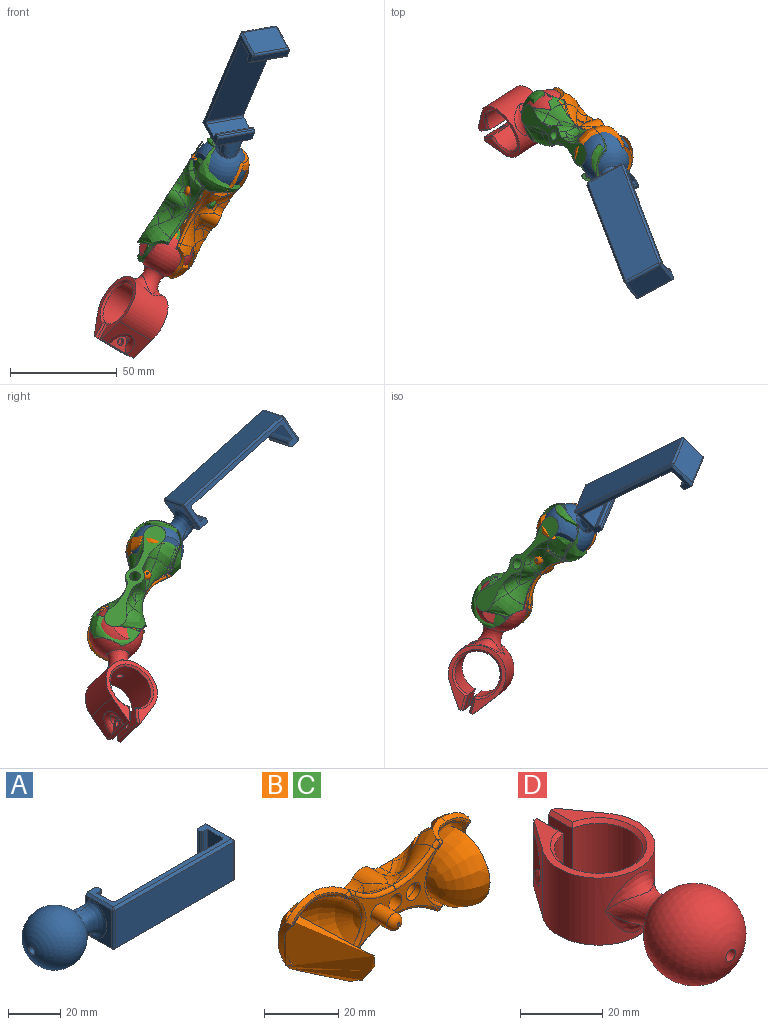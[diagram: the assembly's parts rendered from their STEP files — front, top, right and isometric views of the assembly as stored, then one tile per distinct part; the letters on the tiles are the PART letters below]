
ASSEMBLY  parts=4 mates=4
PART A: 46 faces, bbox 98.6x25.9x25.9 mm
  f0: plane 18.06x11.56mm, normal (-1,0,0), area 79.7mm2, adj f19,f29,f36,f45
  f1: plane 5.66x3.37mm, normal (-1,0,0), area 4.8mm2, adj f8,f20,f45
  f2: sphere r=12.5mm, area 1668.1mm2, adj f3,f18,f19,f20,f21,f22
  f3: plane 15x15mm, normal (0,0,-1), area 176.7mm2, adj f2
  f4: plane 5.66x3.37mm, normal (-1,0,0), area 4.8mm2, adj f8,f21,f36
  f5: plane 20x8mm, normal (1,0,0), area 160mm2, adj f6,f16,f17,f35
  f6: plane 20x2mm, normal (0,-1,0), area 40mm2, adj f5,f16,f17,f27
  f7: plane 20x1mm, normal (1,0,0), area 20mm2, adj f16,f17,f27,f28
  f8: plane 20x5mm, normal (0,1,0), area 99mm2, adj f1,f4,f16,f17,f18,f28,f36,f45
  f9: plane 64x18mm, normal (0,-1,0), area 1152mm2, adj f29,f30,f38,f43
  f10: plane 18x13mm, normal (1,0,0), area 234mm2, adj f30,f31,f40,f41
  f11: plane 20x4mm, normal (0,1,0), area 80mm2, adj f16,f17,f31,f32
  f12: plane 20x1mm, normal (-1,0,0), area 20mm2, adj f16,f17,f32,f33
  f13: plane 20x2mm, normal (0,-1,0), area 40mm2, adj f14,f16,f17,f33
  f14: plane 20x8mm, normal (-1,0,0), area 160mm2, adj f13,f16,f17,f34
  f15: plane 58x20mm, normal (0,1,0), area 1160mm2, adj f16,f17,f34,f35
  f16: plane 64x14mm, normal (0,0,1), area 193.6mm2, adj f5,f6,f7,f8,f11,f12,f13,f14
  f17: plane 64x14mm, normal (0,0,-1), area 193.6mm2, adj f5,f6,f7,f8,f11,f12,f13,f14
  f18: bspline ~14.32x8mm, area 52.9mm2, adj f2,f8,f20,f21
  f19: bspline ~18x13.55mm, area 213.6mm2, adj f0,f2,f20,f21
  f20: bspline ~11.31x8.33mm, area 31.4mm2, adj f1,f2,f18,f19
  f21: bspline ~11.31x8.33mm, area 31.4mm2, adj f2,f4,f18,f19
  f22: cone r=1.62mm half-angle=3deg, axis (-1,0,0), area 33.7mm2, adj f2,f23
  f23: sphere r=9mm, area 804.6mm2, adj f22,f24,f25
  f24: plane 8.83x8.83mm, normal (-1,0,0), area 60.2mm2, adj f23,f26
  f25: plane 12.45x12.45mm, normal (0,0,1), area 121.7mm2, adj f23
  f26: cone r=1.62mm half-angle=3deg, axis (-1,0,0), area 18.7mm2, adj f24
  f27: cylinder r=1mm len=20mm, axis (0,0,1), area 31.4mm2, adj f6,f7,f16,f17
  f28: cylinder r=1mm len=20mm, axis (0,0,-1), area 31.4mm2, adj f7,f8,f16,f17
  f29: cylinder r=1mm len=18mm, axis (0,0,-1), area 28.3mm2, adj f0,f9,f37,f44
  f30: cylinder r=1mm len=18mm, axis (0,0,-1), area 28.3mm2, adj f9,f10,f39,f42
  f31: cylinder r=1mm len=20mm, axis (0,0,-1), area 29.8mm2, adj f10,f11,f40,f41
  f32: cylinder r=1mm len=20mm, axis (0,0,-1), area 31.4mm2, adj f11,f12,f16,f17
  f33: cylinder r=1mm len=20mm, axis (0,0,1), area 31.4mm2, adj f12,f13,f16,f17
  f34: cylinder r=1mm len=20mm, axis (0,0,1), area 31.4mm2, adj f14,f15,f16,f17
  f35: cylinder r=1mm len=20mm, axis (0,0,1), area 31.4mm2, adj f5,f15,f16,f17
  f36: plane 14x1mm, normal (-0.71,0,0.71), area 19.8mm2, adj f0,f4,f8,f16,f37
  f37: cone r=1mm half-angle=45deg, axis (0,0,-1), area 1.1mm2, adj f29,f36,f38
  f38: plane 64x1mm, normal (0,-0.71,0.71), area 90.5mm2, adj f9,f16,f37,f39
  f39: cone r=1mm half-angle=45deg, axis (0,0,-1), area 1.1mm2, adj f30,f38,f40
  f40: plane 14.42x1.42mm, normal (0.71,0,0.71), area 19.5mm2, adj f10,f16,f31,f39
  f41: plane 14.42x1.42mm, normal (0.71,0,-0.71), area 19.5mm2, adj f10,f17,f31,f42
  f42: cone r=1mm half-angle=45deg, axis (0,0,1), area 1.1mm2, adj f30,f41,f43
  f43: plane 64x1mm, normal (0,-0.71,-0.71), area 90.5mm2, adj f9,f17,f42,f44
  f44: cone r=1mm half-angle=45deg, axis (0,0,1), area 1.1mm2, adj f29,f43,f45
  f45: plane 14x1mm, normal (-0.71,0,-0.71), area 19.8mm2, adj f0,f1,f8,f17,f44
PART B: 88 faces, bbox 71.9x25.8x27.9 mm
  f0: cylinder r=0.5mm len=1mm, axis (0,-1,0), area 0.2mm2, adj f86,f87
  f1: plane 59.78x10.4mm, normal (0,-1,0), area 338mm2, adj f2,f3,f8,f14,f15,f16,f17,f19
  f2: plane 4.98x3.76mm, normal (0,0,-1), area 10.1mm2, adj f1,f17,f18,f19
  f3: plane 4.98x3.76mm, normal (0,0,1), area 10.1mm2, adj f1,f22,f23,f24
  f4: revolved ~14.78x8.77mm, area 71.8mm2, adj f8,f22,f24,f26,f40,f78
  f5: plane 9.69x5.17mm, normal (0,1,0), area 6.9mm2, adj f11,f13,f29,f30,f35
  f6: revolved ~22.89x20.47mm, area 471.5mm2, adj f32,f33,f34,f35,f36,f37
  f7: revolved ~14.78x8.77mm, area 71.8mm2, adj f8,f17,f18,f21,f43,f72
  f8: revolved ~27.88x20.27mm, area 464.7mm2, adj f1,f4,f7,f17,f22,f27,f28,f29
  f9: plane 34.64x21.31mm, normal (0,1,0), area 187.2mm2, adj f14,f32,f64,f70,f71,f72,f73,f74
  f10: plane 9.69x5.17mm, normal (0,1,0), area 6.9mm2, adj f12,f13,f28,f29,f36
  f11: cylinder r=6.5mm len=6.41mm, axis (0,0,1), area 5.7mm2, adj f5,f31,f32,f33,f70
  f12: cylinder r=6.5mm len=6.41mm, axis (0,0,1), area 5.7mm2, adj f10,f27,f32,f34,f76
  f13: cylinder r=9mm len=12.45mm, axis (1,0,0), area 11.1mm2, adj f5,f10,f29,f35,f36,f37
  f14: cylinder r=2.5mm len=13mm, axis (0,1,0), area 204.2mm2, adj f1,f9
  f15: cylinder r=4.5mm len=9.88mm, axis (0,1,0), area 50.1mm2, adj f1,f23,f26,f55,f58
  f16: cylinder r=4.5mm len=9.88mm, axis (0,1,0), area 50.1mm2, adj f1,f19,f21,f51,f53
  f17: bspline ~12.49x9.13mm, area 25.5mm2, adj f1,f2,f7,f8,f18
  f18: bspline ~9.56x8.32mm, area 36.1mm2, adj f2,f7,f17,f20
  f19: cylinder r=5mm len=3.75mm, axis (0,1,0), area 15.3mm2, adj f1,f2,f16,f20
  f20: sphere r=5mm, area 20.4mm2, adj f18,f19,f21
  f21: bspline ~10.34x8.54mm, area 33.7mm2, adj f7,f16,f20,f53
  f22: bspline ~13.1x9.66mm, area 25.5mm2, adj f1,f3,f4,f8,f24
  f23: cylinder r=5mm len=3.75mm, axis (0,1,0), area 15.3mm2, adj f1,f3,f15,f25
  f24: bspline ~9.56x8.32mm, area 36.1mm2, adj f3,f4,f22,f25
  f25: sphere r=5mm, area 20.4mm2, adj f23,f24,f26
  f26: bspline ~9.38x7.96mm, area 33.7mm2, adj f4,f15,f25,f58
  f27: bspline ~7.76x6.42mm, area 16mm2, adj f8,f12,f28,f76,f77
  f28: bspline ~11.42x7.33mm, area 19.3mm2, adj f8,f10,f27,f29
  f29: bspline ~15.24x4.31mm, area 27mm2, adj f5,f8,f10,f13,f28,f30
  f30: bspline ~11.42x7.33mm, area 19.3mm2, adj f5,f8,f29,f31
  f31: bspline ~7.76x6.42mm, area 16mm2, adj f8,f11,f30,f70,f71
  f32: bspline ~21.95x7.72mm, area 36.2mm2, adj f6,f9,f11,f12,f33,f34,f70,f76
  f33: bspline ~8.5x6.98mm, area 9.1mm2, adj f6,f11,f32,f35
  f34: bspline ~8.5x6.98mm, area 9.1mm2, adj f6,f12,f32,f36
  f35: bspline ~10.93x5.33mm, area 10mm2, adj f5,f6,f13,f33,f37
  f36: bspline ~10.93x5.33mm, area 10mm2, adj f6,f10,f13,f34,f37
  f37: bspline ~14.29x3.88mm, area 9.7mm2, adj f6,f13,f35,f36
  f38: plane 4.98x3.76mm, normal (0,0,-1), area 10.1mm2, adj f1,f49,f50,f51
  f39: plane 4.98x3.76mm, normal (0,0,1), area 10.1mm2, adj f1,f54,f55,f56
  f40: revolved ~14.78x8.77mm, area 71.8mm2, adj f4,f44,f54,f56,f58,f79
  f41: plane 9.69x5.17mm, normal (0,1,0), area 6.9mm2, adj f46,f48,f61,f62,f67
  f42: revolved ~22.89x20.47mm, area 471.5mm2, adj f64,f65,f66,f67,f68,f69
  f43: revolved ~14.78x8.77mm, area 71.8mm2, adj f7,f44,f49,f50,f53,f73
  f44: revolved ~27.88x20.27mm, area 464.6mm2, adj f1,f40,f43,f49,f54,f59,f60,f61
  f45: plane 9.69x5.17mm, normal (0,1,0), area 6.9mm2, adj f47,f48,f60,f61,f68
  f46: cylinder r=6.5mm len=6.41mm, axis (0,0,1), area 5.7mm2, adj f41,f63,f64,f65,f74
  f47: cylinder r=6.5mm len=6.41mm, axis (0,0,1), area 5.7mm2, adj f45,f59,f64,f66,f81
  f48: cylinder r=9mm len=12.45mm, axis (-1,0,0), area 11.1mm2, adj f41,f45,f61,f67,f68,f69
  f49: bspline ~13.1x9.66mm, area 25.5mm2, adj f1,f38,f43,f44,f50
  f50: bspline ~9.56x8.32mm, area 36.1mm2, adj f38,f43,f49,f52
  f51: cylinder r=5mm len=3.75mm, axis (0,1,0), area 15.3mm2, adj f1,f16,f38,f52
  f52: sphere r=5mm, area 16.3mm2, adj f50,f51,f53
  f53: bspline ~10.05x8.54mm, area 33.7mm2, adj f16,f21,f43,f52
  f54: bspline ~12.49x9.13mm, area 25.5mm2, adj f1,f39,f40,f44,f56
  f55: cylinder r=5mm len=3.75mm, axis (0,1,0), area 15.3mm2, adj f1,f15,f39,f57
  f56: bspline ~9.56x8.32mm, area 36.1mm2, adj f39,f40,f54,f57
  f57: sphere r=5mm, area 20.4mm2, adj f55,f56,f58
  f58: bspline ~9.72x7.96mm, area 33.7mm2, adj f15,f26,f40,f57
  f59: bspline ~7.97x7.55mm, area 16mm2, adj f44,f47,f60,f80,f81
  f60: bspline ~11.42x7.33mm, area 19.3mm2, adj f44,f45,f59,f61
  f61: bspline ~15.99x4.66mm, area 27mm2, adj f41,f44,f45,f48,f60,f62
  f62: bspline ~10.29x5.59mm, area 19.3mm2, adj f41,f44,f61,f63
  f63: bspline ~7.76x6.42mm, area 16mm2, adj f44,f46,f62,f74,f75
  f64: bspline ~21.95x7.72mm, area 36.2mm2, adj f9,f42,f46,f47,f65,f66,f74,f81
  f65: bspline ~8.5x6.98mm, area 9.1mm2, adj f42,f46,f64,f67
  f66: bspline ~8.5x6.98mm, area 9.1mm2, adj f42,f47,f64,f68
  f67: bspline ~10.93x5.33mm, area 10mm2, adj f41,f42,f48,f65,f69
  f68: bspline ~10.93x5.33mm, area 10mm2, adj f42,f45,f48,f66,f69
  f69: bspline ~14.29x3.88mm, area 9.7mm2, adj f42,f48,f67,f68
  f70: bspline ~2.26x1.82mm, area 1.9mm2, adj f9,f11,f31,f32,f71
  f71: bspline ~3.63x3.01mm, area 3.6mm2, adj f8,f9,f31,f70,f72
  f72: bspline ~21.28x7mm, area 28.5mm2, adj f7,f8,f9,f71,f73
  f73: bspline ~21.28x7mm, area 28.5mm2, adj f9,f43,f44,f72,f75
  f74: bspline ~2.41x1.9mm, area 1.9mm2, adj f9,f46,f63,f64,f75
  f75: bspline ~3.63x3.01mm, area 3.6mm2, adj f9,f44,f63,f73,f74
  f76: bspline ~2.26x1.82mm, area 1.9mm2, adj f9,f12,f27,f32,f77
  f77: bspline ~3.63x3.01mm, area 3.6mm2, adj f8,f9,f27,f76,f78
  f78: bspline ~21.28x7mm, area 28.5mm2, adj f4,f8,f9,f77,f79
  f79: bspline ~21.28x7mm, area 28.5mm2, adj f9,f40,f44,f78,f80
  f80: bspline ~3.63x3.01mm, area 3.6mm2, adj f9,f44,f59,f79,f81
  f81: bspline ~2.41x1.9mm, area 1.9mm2, adj f9,f47,f59,f64,f80
  f82: cylinder r=2.5mm len=6mm, axis (0,1,0), area 94.2mm2, adj f9,f84
  f83: plane 1x1mm, normal (0,1,0), area 0.8mm2, adj f84
  f84: torus R=0.5mm, axis (0,-1,0), area 35mm2, adj f82,f83
  f85: cylinder r=2.7mm len=5.4mm, axis (0,-1,0), area 33.9mm2, adj f9,f86
  f86: torus R=0.5mm, axis (0,-1,0), area 41.3mm2, adj f0,f85
  f87: plane 1x1mm, normal (0,1,0), area 0.8mm2, adj f0
PART C: same geometry as B
PART D: 34 faces, bbox 27.5x64.3x25 mm
  f0: cylinder r=10.75mm len=21.5mm, axis (0,0,-1), area 1153.3mm2, adj f6,f7,f23,f29,f32
  f1: cylinder r=13.75mm len=27.5mm, axis (0,0,-1), area 1205.2mm2, adj f3,f4,f9,f10,f19,f20
  f2: cylinder r=1.62mm len=3.25mm, axis (1,0,0), area 20.4mm2, adj f7,f13
  f3: plane 20x10.76mm, normal (-0.81,0.58,0), area 162.4mm2, adj f1,f8,f9,f10,f17
  f4: plane 20x10.76mm, normal (0.81,0.58,0), area 162.4mm2, adj f1,f5,f9,f10,f16
  f5: plane 20x2mm, normal (0,1,0), area 39mm2, adj f4,f6,f9,f10,f15,f30,f31
  f6: plane 18x8.11mm, normal (-1,0,0), area 137.6mm2, adj f0,f5,f11,f30,f31
  f7: plane 18x8.11mm, normal (1,0,0), area 137.6mm2, adj f0,f2,f8,f28,f33
  f8: plane 20x2mm, normal (0,1,0), area 39mm2, adj f3,f7,f9,f10,f13,f28,f33
  f9: plane 32.5x27.5mm, normal (0,0,1), area 192.5mm2, adj f1,f3,f4,f5,f8,f31,f32,f33
  f10: plane 32.5x27.5mm, normal (0,0,-1), area 192.5mm2, adj f1,f3,f4,f5,f8,f28,f29,f30
  f11: cylinder r=1.62mm len=3.25mm, axis (1,0,0), area 20.4mm2, adj f6,f15
  f12: cylinder r=3.25mm len=6.27mm, axis (1,0,0), area 0mm2, adj f13,f17
  f13: plane 12x6.75mm, normal (-1,0,0), area 37mm2, adj f2,f8,f12,f17
  f14: cylinder r=3.25mm len=6.27mm, axis (-1,0,0), area 0mm2, adj f15,f16
  f15: plane 12x6.75mm, normal (1,0,0), area 37mm2, adj f5,f11,f14,f16
  f16: bspline ~12.5x8.2mm, area 68.7mm2, adj f4,f14,f15
  f17: bspline ~12.5x8.2mm, area 68.7mm2, adj f3,f12,f13
  f18: revolved ~16.85x16.85mm, area 232.1mm2, adj f19,f20,f21
  f19: bspline ~16.85x8.55mm, area 0mm2, adj f1,f18
  f20: bspline ~16.85x8.55mm, area 0mm2, adj f1,f18
  f21: sphere r=12.5mm, area 1668.1mm2, adj f18,f22,f24
  f22: plane 15x15mm, normal (0,0,-1), area 176.7mm2, adj f21
  f23: cylinder r=1.62mm len=14.5mm, axis (0,-1,0), area 148mm2, adj f0,f26
  f24: cylinder r=1.62mm len=3.54mm, axis (0,-1,0), area 36.2mm2, adj f21,f25
  f25: sphere r=9mm, area 802.8mm2, adj f24,f26,f27
  f26: plane 8.83x8.83mm, normal (0,-1,0), area 52.9mm2, adj f23,f25
  f27: plane 12.45x12.45mm, normal (0,0,1), area 121.7mm2, adj f25
  f28: plane 8.14x1.03mm, normal (0.71,0,-0.71), area 10.9mm2, adj f7,f8,f10,f29
  f29: cone r=11.75mm half-angle=45deg, axis (0,0,-1), area 94.3mm2, adj f0,f10,f28,f30
  f30: plane 8.14x1.03mm, normal (-0.71,0,-0.71), area 10.9mm2, adj f5,f6,f10,f29
  f31: plane 8.14x1.03mm, normal (-0.71,0,0.71), area 10.9mm2, adj f5,f6,f9,f32
  f32: cone r=10.75mm half-angle=45deg, axis (0,0,1), area 94.3mm2, adj f0,f9,f31,f33
  f33: plane 8.14x1.03mm, normal (0.71,0,0.71), area 10.9mm2, adj f7,f8,f9,f32
PLACE A rot(axis=(-0.73,0.14,-0.67),122.9deg) t=(-8.48,-36.08,-21.37)mm
PLACE B rot(axis=(0.43,0.79,-0.44),146.4deg) t=(-27.82,-11.15,-55.49)mm
PLACE C rot(axis=(-0.23,0.63,0.74),125.5deg) t=(-26.12,-10.89,-56.44)mm
PLACE D rot(axis=(-0.8,0.55,-0.23),122deg) t=(-55.19,-3.81,-104.74)mm
MATE ball B.f4 <-> D.f21  axis (0.5,-0.37,0.78) through (-39.53,-1.36,-75.69)mm
MATE ball D.f21 <-> C.f4  axis (0.75,0.49,-0.45) through (-39.53,-1.36,-75.69)mm
MATE ball C.f4 <-> A.f2  axis (-0.5,0.37,-0.78) through (-14.37,-20.33,-36.09)mm
MATE ball B.f4 <-> A.f2  axis (-0.5,0.37,-0.78) through (-14.37,-20.33,-36.09)mm
